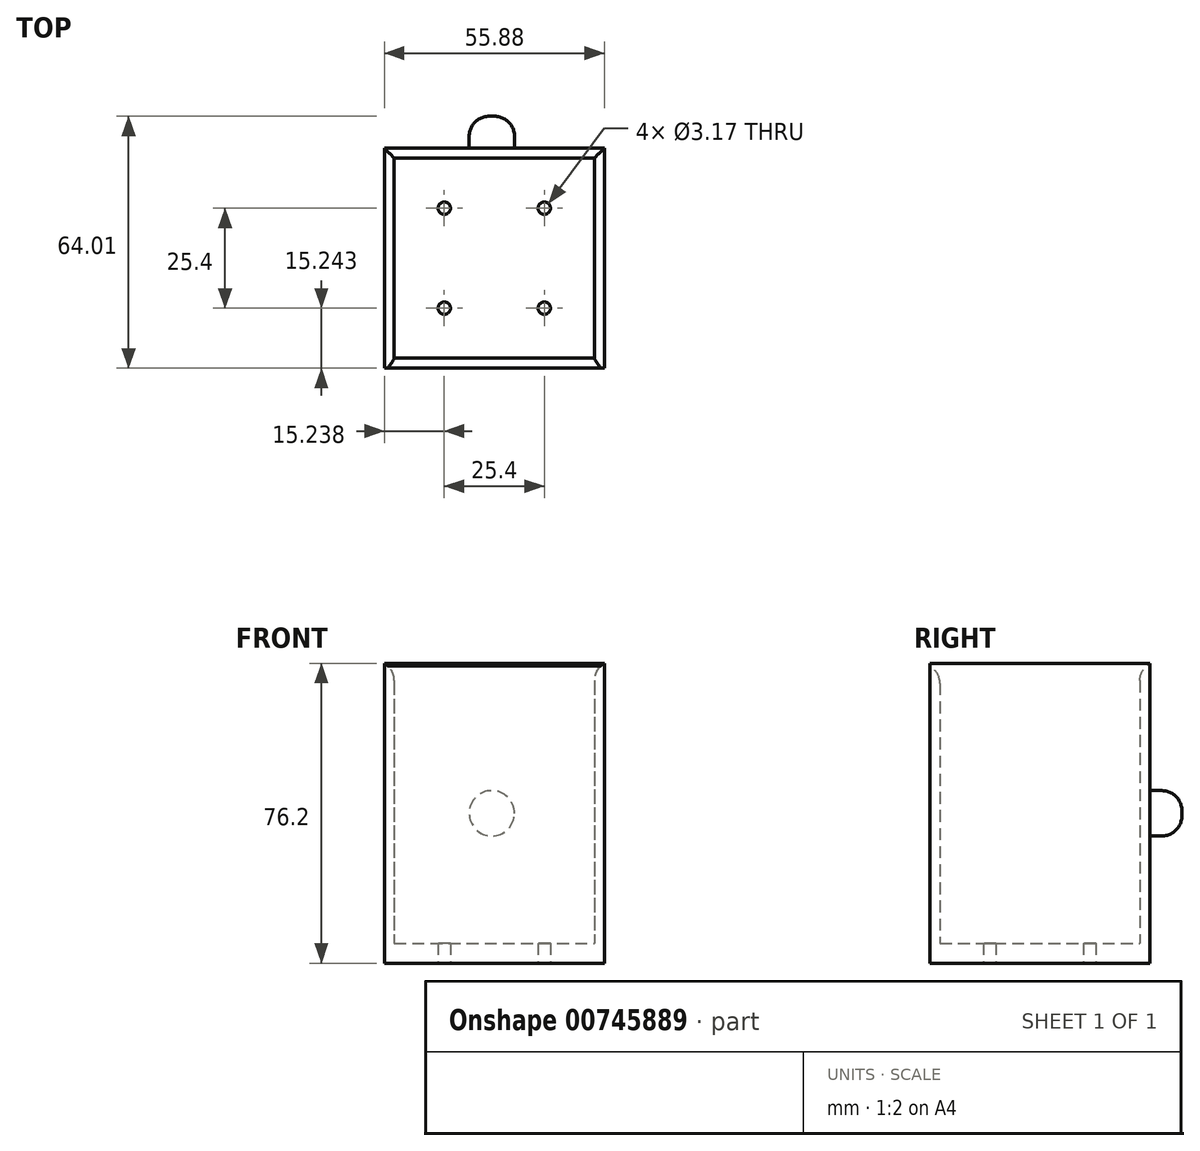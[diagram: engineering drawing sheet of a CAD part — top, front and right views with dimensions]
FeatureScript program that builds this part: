
annotation { "Feature Type Name" : "Feature", "Feature Type Description" : "" }
export const myFeature = defineFeature(function(context is Context, id is Id, definition is map)
    precondition{}
    {
        {
            var Q0;
            Q0=qCreatedBy(makeId("Top.planeOp"),FACE);
            var sketch = newSketch(context, id + "F0", { "sketchPlane" : qUnion([Q0])});
            skLineSegment(sketch, "E0.bottom", {"start": v(-24.77, -26.2) * mm, "end": v(26.03, -26.2) * mm});
            skLineSegment(sketch, "E0.top", {"start": v(-24.77, 24.6) * mm, "end": v(26.03, 24.6) * mm});
            skLineSegment(sketch, "E0.left", {"start": v(-24.77, -26.2) * mm, "end": v(-24.77, 24.6) * mm});
            skLineSegment(sketch, "E0.right", {"start": v(26.03, -26.2) * mm, "end": v(26.03, 24.6) * mm});
            skLineSegment(sketch, "E1.bottom", {"start": v(-27.31, -28.75) * mm, "end": v(28.57, -28.75) * mm});
            skLineSegment(sketch, "E1.top", {"start": v(-27.31, 27.13) * mm, "end": v(28.57, 27.13) * mm});
            skLineSegment(sketch, "E1.left", {"start": v(-27.31, -28.75) * mm, "end": v(-27.31, 27.13) * mm});
            skLineSegment(sketch, "E1.right", {"start": v(28.57, -28.75) * mm, "end": v(28.57, 27.13) * mm});
            skCircle(sketch, "E2", {"center": v(-12.07, 11.9) * mm, "radius": 1.59 * mm});
            skCircle(sketch, "E3", {"center": v(-12.07, -13.5) * mm, "radius": 1.59 * mm});
            skCircle(sketch, "E4", {"center": v(13.33, -13.5) * mm, "radius": 1.59 * mm});
            skCircle(sketch, "E5", {"center": v(13.33, 11.9) * mm, "radius": 1.59 * mm});
            skSolve(sketch);
        }
        {
            var Q0;
            Q0=makeQuery(id+"F0.imprint","IMPRINT",FACE,{"disambiguationData":[TD([[makeQuery(id+"F0.imprint","IMPRINT",EDGE,{"derivedFrom":sQuery(id+"F0.wireOp",EDGE,"E0.bottom")}),1.0]])]});
            extrude(context, id + "F1", {"entities" : qUnion([Q0]), "depth" : 5.08 * mm, "offsetDistance" : 25.4 * mm});
        }
        {
            var Q0;
            Q0 = qSketchRegion(id + "F0", true);
            extrude(context, id + "F2", {"entities" : qUnion([Q0]), "operationType" : NewBodyOperationType.ADD, "depth" : 76.2 * mm, "offsetDistance" : 25.4 * mm});
        }
        {
            var Q0;
            Q0=makeQuery(id+"F2.opExtrude","CAP_EDGE",EDGE,{"disambiguationData":[OSD([sQuery(id+"F0.wireOp",EDGE,"E0.bottom")])],"isStart":false});
            fillet(context, id + "F3", {"entities" : qUnion([Q0]), "radius" : 5.08 * mm, "tangentPropagation" : true, "allowEdgeOverflow" : false});
        }
        {
            var Q0;
            Q0=makeQuery(id+"F2.opExtrude","CAP_EDGE",EDGE,{"disambiguationData":[OSD([sQuery(id+"F0.wireOp",EDGE,"E0.left")])],"isStart":false});
            fillet(context, id + "F4", {"entities" : qUnion([Q0]), "radius" : 5.08 * mm, "tangentPropagation" : true, "allowEdgeOverflow" : false});
        }
        {
            var Q0;
            Q0=makeQuery(id+"F2.opExtrude","CAP_EDGE",EDGE,{"disambiguationData":[OSD([sQuery(id+"F0.wireOp",EDGE,"E0.top")])],"isStart":false});
            fillet(context, id + "F5", {"entities" : qUnion([Q0]), "radius" : 5.08 * mm, "tangentPropagation" : true, "allowEdgeOverflow" : false});
        }
        {
            var Q0;
            Q0=makeQuery(id+"F2.opExtrude","CAP_EDGE",EDGE,{"disambiguationData":[OSD([sQuery(id+"F0.wireOp",EDGE,"E0.right")])],"isStart":false});
            fillet(context, id + "F6", {"entities" : qUnion([Q0]), "radius" : 5.08 * mm, "tangentPropagation" : true, "allowEdgeOverflow" : false});
        }
        {
            var Q0;
            Q0=makeQuery(id+"F2.opExtrude","SWEPT_FACE",FACE,{"disambiguationData":[OSD([sQuery(id+"F0.wireOp",EDGE,"E1.top")])]});
            var sketch = newSketch(context, id + "F7", { "sketchPlane" : qUnion([Q0])});
            skCircle(sketch, "E6", {"center": v(0, 38.1) * mm, "radius": 5.76 * mm});
            skSolve(sketch);
        }
        {
            var Q0;
            Q0=makeQuery(id+"F7.imprint","IMPRINT",FACE,{"disambiguationData":[TD([[makeQuery(id+"F7.imprint","IMPRINT",EDGE,{"derivedFrom":sQuery(id+"F7.wireOp",EDGE,"E6")}),1.0]])]});
            extrude(context, id + "F8", {"entities" : qUnion([Q0]), "operationType" : NewBodyOperationType.ADD, "depth" : 8.13 * mm, "offsetDistance" : 25.4 * mm});
        }
        {
            var Q0;
            Q0=makeQuery(id+"F8.opExtrude","CAP_EDGE",EDGE,{"disambiguationData":[OSD([sQuery(id+"F7.wireOp",EDGE,"E6")])],"isStart":false});
            fillet(context, id + "F9", {"entities" : qUnion([Q0]), "radius" : 5.08 * mm, "tangentPropagation" : true, "allowEdgeOverflow" : false});
        }
    });
